# Revit family: Electronics_Huddle-Room-Solutions_Biamp_Devio_Beamtracking-Tabletop-Microphone_DTM-1__
name_source: partatom
category: Communication Devices
units: mm (PartAtom-declared; Revit-internal decimal feet)

## family parameters
Cut with Voids When Loaded = No
Host = Face
Maintain Annotation Orientation = No
OmniClass Number = 23.85.10.11.14.14.11
OmniClass Title = Microphones
Part Type = Normal
Room Calculation Point = No
Round Connector Dimension = Use Diameter
Shared = No

## types (1)
- DTM-1
    Altitude = 0-6,600 ft (0-2000m) MSL
    Automatic Noise Suppression = 4 modes: Of, Low (Default), Medium, High
    Compliance = FCC Part 15B (USA); CE marked (Europe); UL and C-UL listed (USA and Canada); RoHS Directive (Europe)
    Connectors = Two RJ-45: one between DTM-1 and Devio SCR-20/SCR-25, the other between DTM-1 and additional DTM
    Default Elevation = 48 "
    Depth = 4.77 "
    Description = Devio® DTM-1 Beamtracking™ Tabletop Microphone
    Digital Interface = Custom/Proprietary
    Dynamic Range = THD+N < 10%: 92 dB, A-Weighted
    Frequency Response = 150 Hz - 16 kHz: ± 3 dB
    Height = 2.2 "
    Housing Material = Biamp - Plastic - Black
    Humidity = 0-95% relative humidity (non-condensing)
    Indicators = Mute Indicator (Green/Red LED)
    Manufacturer = Biamp
    Max Distance Between Devices = 49 feet (15 meters) from SCR-20/SCR-25 to DTM-1; 49 feet (15 meters) for daisy-chained connections between DTM-1 microphones
    Maximum SPL = 0.5% THD: 106 dB SPL
    Microphone Technology = 8-Element Digital Array
    Model = Devio DTM-1
    Mute Switching = 3 Capacitive Touch Buttons
    Polar Pattern = Active Beamformed
    Power = < 1 W, phantom powered from SCR-20/SCR-25
    Product Documentation Link = https://downloads.biamp.com
    Product Page URL = https://www.biamp.com
    Product data url = https://www.bimobject.com
    Selectable Directivity Modes = 2 modes: Middle of Table (360°) or End of Table (120°)
    Sensitivity = 94 dB SPL, 1 kHz: > 70 dB, A-Weighted
    Temperature Range = 32 - 104° F (0 - 40° C)
    URL = https://www.biamp.com
    Weight = 0.60 lbf
    Width = 5.13 "

## geometry (parser evidence)
native form markers: Sweep x2
no freeform markers — native parametric forms only
